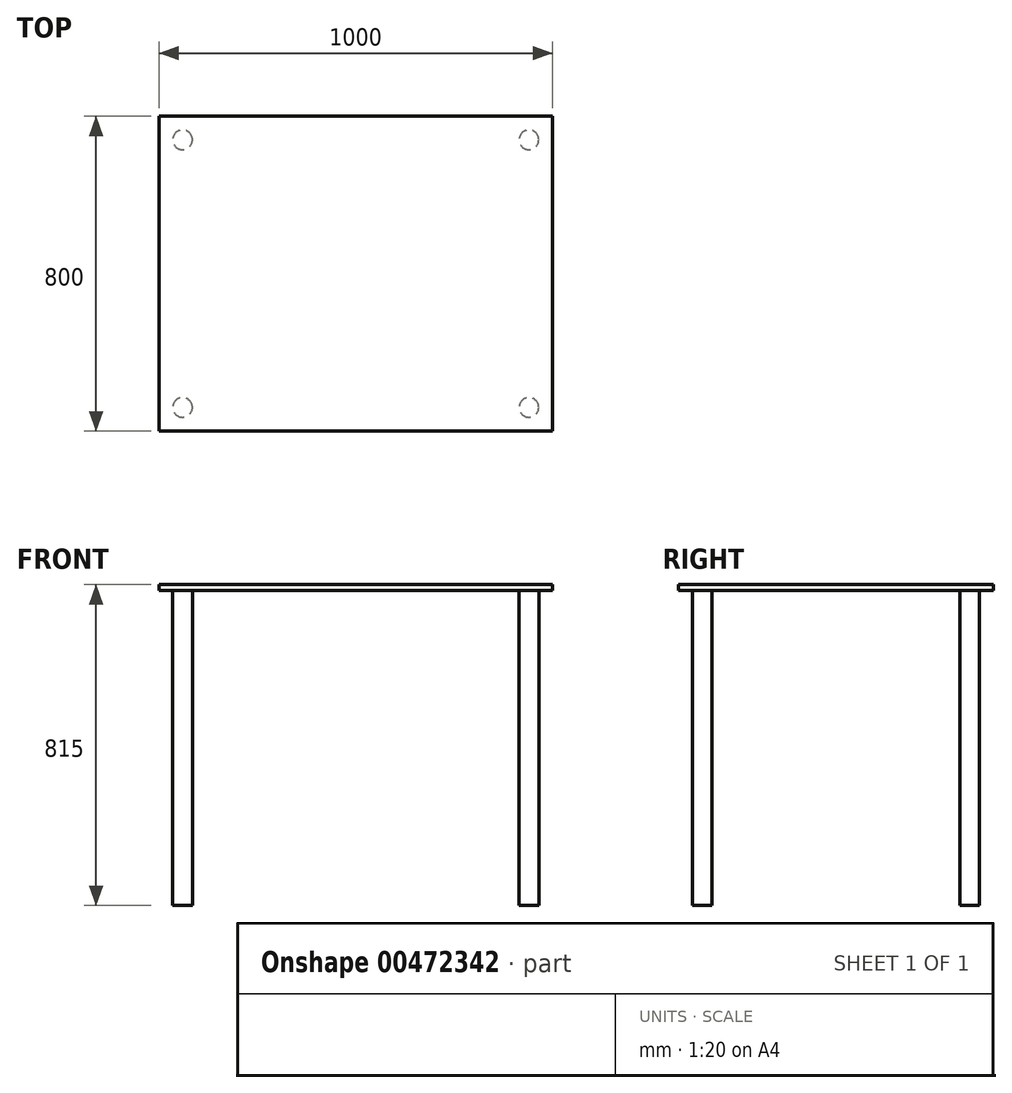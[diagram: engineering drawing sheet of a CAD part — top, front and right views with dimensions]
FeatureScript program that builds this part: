
annotation { "Feature Type Name" : "Feature", "Feature Type Description" : "" }
export const myFeature = defineFeature(function(context is Context, id is Id, definition is map)
    precondition{}
    {
        {
            var Q0;
            Q0=qCreatedBy(makeId("Top.planeOp"),FACE);
            var sketch = newSketch(context, id + "F0", { "sketchPlane" : qUnion([Q0])});
            skLineSegment(sketch, "E0.bottom", {"start": v(-500, 400) * mm, "end": v(500, 400) * mm});
            skLineSegment(sketch, "E0.top", {"start": v(-500, -400) * mm, "end": v(500, -400) * mm});
            skLineSegment(sketch, "E0.left", {"start": v(-500, 400) * mm, "end": v(-500, -400) * mm});
            skLineSegment(sketch, "E0.right", {"start": v(500, 400) * mm, "end": v(500, -400) * mm});
            skSolve(sketch);
        }
        {
            var Q0;
            Q0=makeQuery(id+"F0.imprint","IMPRINT",FACE,{"disambiguationData":[TD([[makeQuery(id+"F0.imprint","IMPRINT",EDGE,{"derivedFrom":sQuery(id+"F0.wireOp",EDGE,"E0.bottom")}),-1.0]])]});
            extrude(context, id + "F1", {"entities" : qUnion([Q0]), "endBound" : BoundingType.SYMMETRIC, "oppositeDirection" : true, "depth" : 15 * mm});
        }
        {
            var Q0;
            Q0=makeQuery(id+"F1.opExtrude","CAP_FACE",FACE,{"disambiguationData":[OSD([sQuery(id+"F0.wireOp",EDGE,"E0.bottom"),sQuery(id+"F0.wireOp",EDGE,"E0.top"),sQuery(id+"F0.wireOp",EDGE,"E0.left"),sQuery(id+"F0.wireOp",EDGE,"E0.right")])],"isStart":false});
            var sketch = newSketch(context, id + "F2", { "sketchPlane" : qUnion([Q0])});
            skCircle(sketch, "E1", {"center": v(-440, 340) * mm, "radius": 25 * mm});
            skCircle(sketch, "E2", {"center": v(-440, -340) * mm, "radius": 25 * mm});
            skCircle(sketch, "E3", {"center": v(440, -340) * mm, "radius": 25 * mm});
            skCircle(sketch, "E4", {"center": v(440, 340) * mm, "radius": 25 * mm});
            skSolve(sketch);
        }
        {
            var Q0;
            Q0 = qSketchRegion(id + "F2", true);
            extrude(context, id + "F3", {"entities" : qUnion([Q0]), "depth" : 800 * mm});
        }
    });
